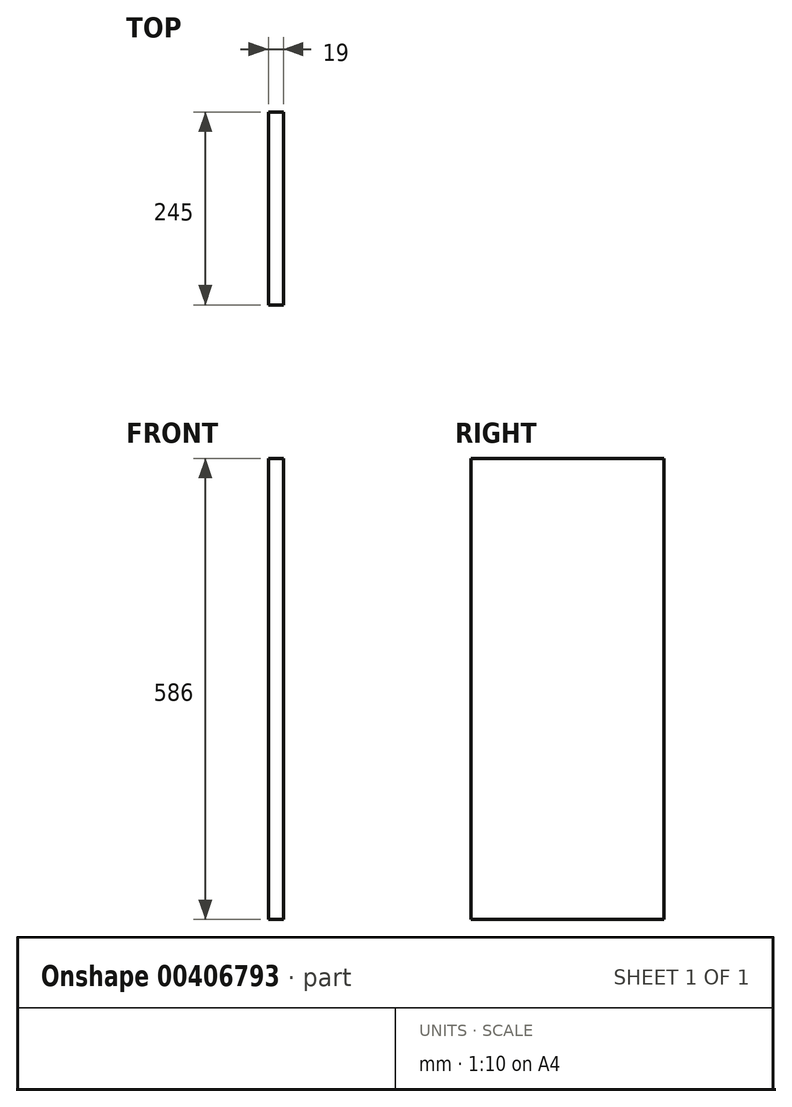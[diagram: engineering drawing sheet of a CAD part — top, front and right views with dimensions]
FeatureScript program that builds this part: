
annotation { "Feature Type Name" : "Feature", "Feature Type Description" : "" }
export const myFeature = defineFeature(function(context is Context, id is Id, definition is map)
    precondition{}
    {
        {
            var Q0;
            Q0=qCreatedBy(makeId("Right.planeOp"),FACE);
            var sketch = newSketch(context, id + "F0", { "sketchPlane" : qUnion([Q0])});
            skLineSegment(sketch, "E0.bottom", {"start": v(0, 0) * mm, "end": v(245, 0) * mm});
            skLineSegment(sketch, "E0.top", {"start": v(0, 586) * mm, "end": v(245, 586) * mm});
            skLineSegment(sketch, "E0.left", {"start": v(0, 0) * mm, "end": v(0, 586) * mm});
            skLineSegment(sketch, "E0.right", {"start": v(245, 0) * mm, "end": v(245, 586) * mm});
            skSolve(sketch);
        }
        {
            var Q0;
            Q0=makeQuery(id+"F0.imprint","IMPRINT",FACE,{"disambiguationData":[TD([[makeQuery(id+"F0.imprint","IMPRINT",EDGE,{"derivedFrom":sQuery(id+"F0.wireOp",EDGE,"E0.bottom")}),1.0]])]});
            extrude(context, id + "F1", {"entities" : qUnion([Q0]), "depth" : 19 * mm, "offsetDistance" : 25 * mm});
        }
    });
